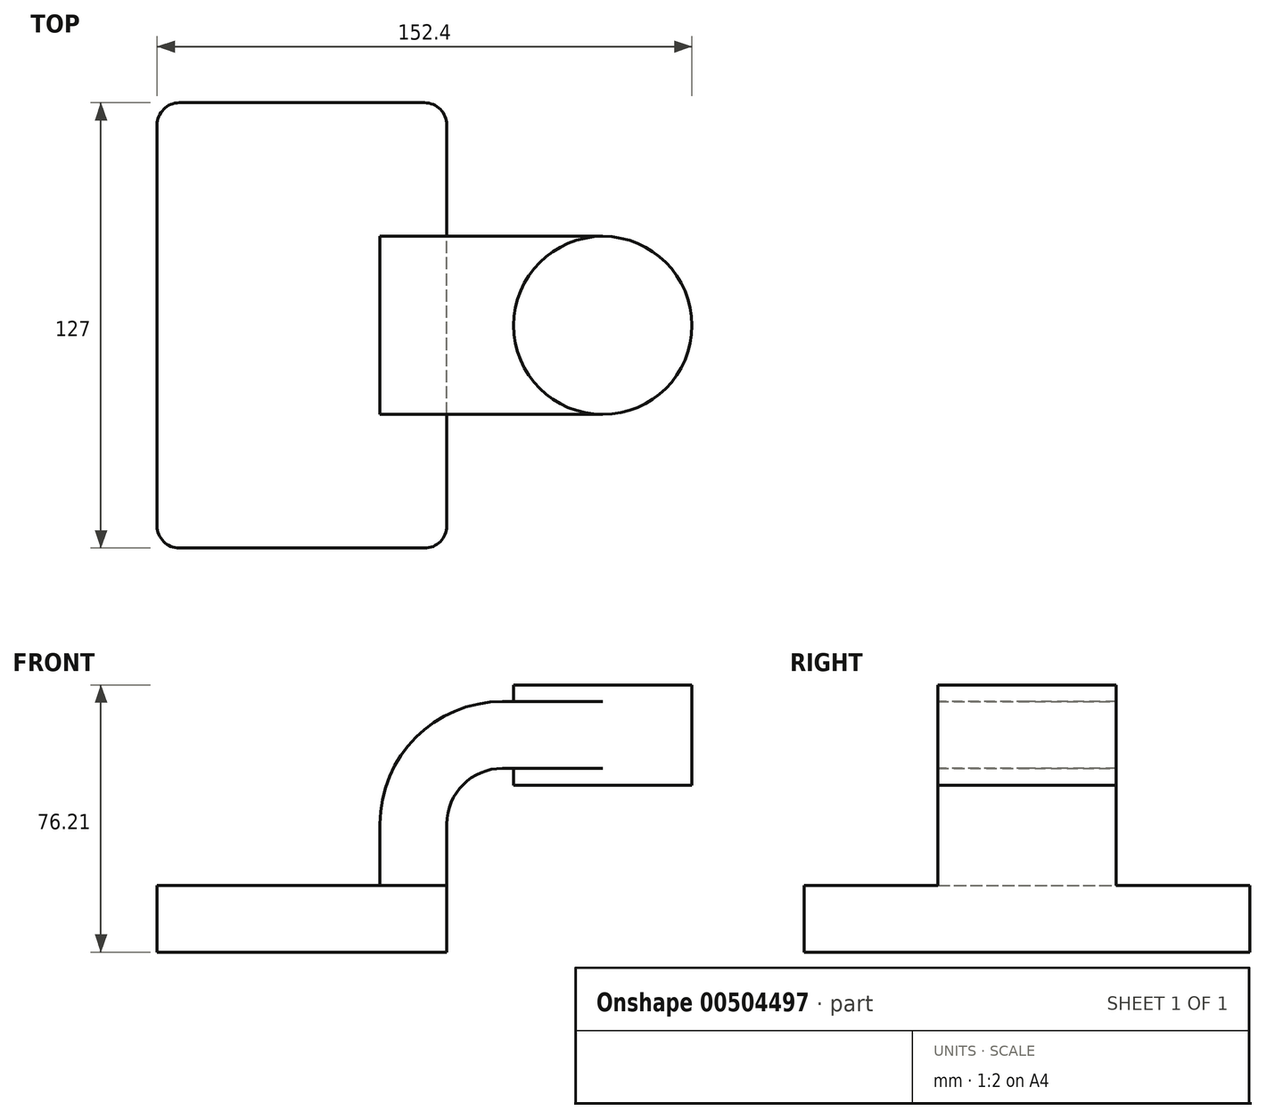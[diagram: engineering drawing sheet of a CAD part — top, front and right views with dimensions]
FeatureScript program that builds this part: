
annotation { "Feature Type Name" : "Feature", "Feature Type Description" : "" }
export const myFeature = defineFeature(function(context is Context, id is Id, definition is map)
    precondition{}
    {
        {
            var Q0;
            Q0=qCreatedBy(makeId("Front.planeOp"),FACE);
            var sketch = newSketch(context, id + "F0", { "sketchPlane" : qUnion([Q0])});
            skLineSegment(sketch, "E0.bottom", {"start": v(-41.28, 9.52) * mm, "end": v(41.27, 9.53) * mm});
            skLineSegment(sketch, "E0.top", {"start": v(-41.28, -9.53) * mm, "end": v(41.28, -9.53) * mm});
            skLineSegment(sketch, "E0.left", {"start": v(-41.28, 9.52) * mm, "end": v(-41.28, -9.53) * mm});
            skLineSegment(sketch, "E0.right", {"start": v(41.27, 9.53) * mm, "end": v(41.28, -9.52) * mm});
            skPoint(sketch, "E0.middle", {"position": v(0, 0) * mm});
            skLineSegment(sketch, "E1.bottom", {"start": v(111.12, 66.68) * mm, "end": v(60.32, 66.68) * mm});
            skLineSegment(sketch, "E1.top", {"start": v(111.12, 38.1) * mm, "end": v(60.32, 38.1) * mm});
            skLineSegment(sketch, "E1.left", {"start": v(111.12, 66.68) * mm, "end": v(111.12, 38.1) * mm});
            skLineSegment(sketch, "E1.right", {"start": v(60.32, 66.67) * mm, "end": v(60.32, 38.1) * mm});
            skPoint(sketch, "E1.middle", {"position": v(85.72, 52.39) * mm});
            skLineSegment(sketch, "E2", {"start": v(41.27, 9.53) * mm, "end": v(41.27, 27) * mm});
            skArc(sketch, "E3", {"start": v(41.27, 27) * mm, "mid": v(45.92, 38.23) * mm, "end": v(57.15, 42.88) * mm});
            skLineSegment(sketch, "E4", {"start": v(57.15, 42.88) * mm, "end": v(85.72, 42.88) * mm});
            skLineSegment(sketch, "E5.0", {"start": v(57.15, 61.93) * mm, "end": v(85.72, 61.93) * mm});
            skArc(sketch, "E5.1", {"start": v(22.22, 27) * mm, "mid": v(32.45, 51.7) * mm, "end": v(57.15, 61.93) * mm});
            skLineSegment(sketch, "E5.2", {"start": v(22.22, 9.53) * mm, "end": v(22.22, 27) * mm});
            skLineSegment(sketch, "E6", {"start": v(85.72, 38.1) * mm, "end": v(85.72, 66.68) * mm});
            skFitSpline(sketch, "E7", {"points": [v(-41.28, 9.52) * mm, v(57.15, 61.93) * mm], "startDerivative": vector(0.98, 51.64) * mm, "endDerivative": vector(114.06, -5.43) * mm});
            skSolve(sketch);
        }
        {
            var Q0;
            Q0=makeQuery(id+"F0.imprint","IMPRINT",FACE,{"disambiguationData":[TD([[makeQuery(id+"F0.imprint","IMPRINT",EDGE,{"derivedFrom":sQuery(id+"F0.wireOp",EDGE,"E0.top")}),1.0]])]});
            extrude(context, id + "F1", {"entities" : qUnion([Q0]), "endBound" : BoundingType.SYMMETRIC, "depth" : 127 * mm});
        }
        {
            var Q0;
            {var subQ1=sQuery(id+"F0.wireOp",EDGE,"E2");Q0=makeQuery(id+"F0.imprint","IMPRINT",FACE,{"disambiguationData":[TD([[makeQuery(id+"F0.imprint","IMPRINT",EDGE,{"derivedFrom":subQ1}),1.0]])]});}
            var Q1;
            {var subQ0=sQuery(id+"F0.wireOp",EDGE,"E5.0");var subQ1=sQuery(id+"F0.wireOp",EDGE,"E1.right");var subQ2=makeQuery(id+"F0.imprint","INTERSECT",VERTEX,{"derivedFrom":[subQ1,subQ0]});Q1=makeQuery(id+"F0.imprint","IMPRINT",FACE,{"disambiguationData":[TD([[makeQuery(id+"F0.imprint","IMPRINT",EDGE,{"disambiguationData":[TD([[subQ2,-1.0]])],"derivedFrom":subQ1}),1.0]])]});}
            extrude(context, id + "F2", {"entities" : qUnion([Q0, Q1]), "operationType" : NewBodyOperationType.ADD, "endBound" : BoundingType.SYMMETRIC, "depth" : 50.8 * mm});
        }
        {
            var Q0;
            Q0=makeQuery(id+"F0.imprint","IMPRINT",FACE,{"disambiguationData":[TD([[makeQuery(id+"F0.imprint","IMPRINT",EDGE,{"derivedFrom":sQuery(id+"F0.wireOp",EDGE,"E5.1")}),1.0]])]});
            extrude(context, id + "F3", {"entities" : qUnion([Q0]), "operationType" : NewBodyOperationType.ADD, "endBound" : BoundingType.SYMMETRIC, "depth" : 15.88 * mm});
        }
        {
            var Q0;
            {var subQ4=sQuery(id+"F0.wireOp",EDGE,"E1.left");Q0=makeQuery(id+"F0.imprint","IMPRINT",FACE,{"disambiguationData":[TD([[makeQuery(id+"F0.imprint","IMPRINT",EDGE,{"derivedFrom":subQ4}),-1.0]])]});}
            var Q1;
            Q1=sQuery(id+"F0.wireOp",EDGE,"E6");
            revolve(context, id + "F4", {"operationType" : NewBodyOperationType.ADD, "entities" : qUnion([Q0]), "axis" : qUnion([Q1]), "revolveType" : RevolveType.FULL});
        }
        {
            var Q0;
            Q0=makeQuery(id+"F1.opExtrude","CAP_EDGE",EDGE,{"disambiguationData":[OSD([sQuery(id+"F0.wireOp",EDGE,"E0.right")])],"isStart":false});
            var Q1;
            Q1=makeQuery(id+"F1.opExtrude","CAP_EDGE",EDGE,{"disambiguationData":[OSD([sQuery(id+"F0.wireOp",EDGE,"E0.right")])],"isStart":true});
            var Q2;
            Q2=makeQuery(id+"F1.opExtrude","CAP_EDGE",EDGE,{"disambiguationData":[OSD([sQuery(id+"F0.wireOp",EDGE,"E0.left")])],"isStart":true});
            var Q3;
            Q3=makeQuery(id+"F1.opExtrude","CAP_EDGE",EDGE,{"disambiguationData":[OSD([sQuery(id+"F0.wireOp",EDGE,"E0.left")])],"isStart":false});
            fillet(context, id + "F5", {"entities" : qUnion([Q0, Q1, Q2, Q3]), "radius" : 6.35 * mm, "tangentPropagation" : true, "allowEdgeOverflow" : false});
        }
        {
            var Q0;
            {var subQ1=sQuery(id+"F0.wireOp",EDGE,"E2");Q0=makeQuery(id+"F0.imprint","IMPRINT",FACE,{"disambiguationData":[TD([[makeQuery(id+"F0.imprint","IMPRINT",EDGE,{"derivedFrom":subQ1}),1.0]])]});}
            var Q1;
            {var subQ0=sQuery(id+"F0.wireOp",EDGE,"E5.0");var subQ1=sQuery(id+"F0.wireOp",EDGE,"E1.right");var subQ2=makeQuery(id+"F0.imprint","INTERSECT",VERTEX,{"derivedFrom":[subQ1,subQ0]});Q1=makeQuery(id+"F0.imprint","IMPRINT",FACE,{"disambiguationData":[TD([[makeQuery(id+"F0.imprint","IMPRINT",EDGE,{"disambiguationData":[TD([[subQ2,-1.0]])],"derivedFrom":subQ1}),1.0]])]});}
            extrude(context, id + "F6", {"entities" : qUnion([Q0, Q1]), "operationType" : NewBodyOperationType.ADD, "endBound" : BoundingType.SYMMETRIC, "depth" : 50.8 * mm});
        }
    });
